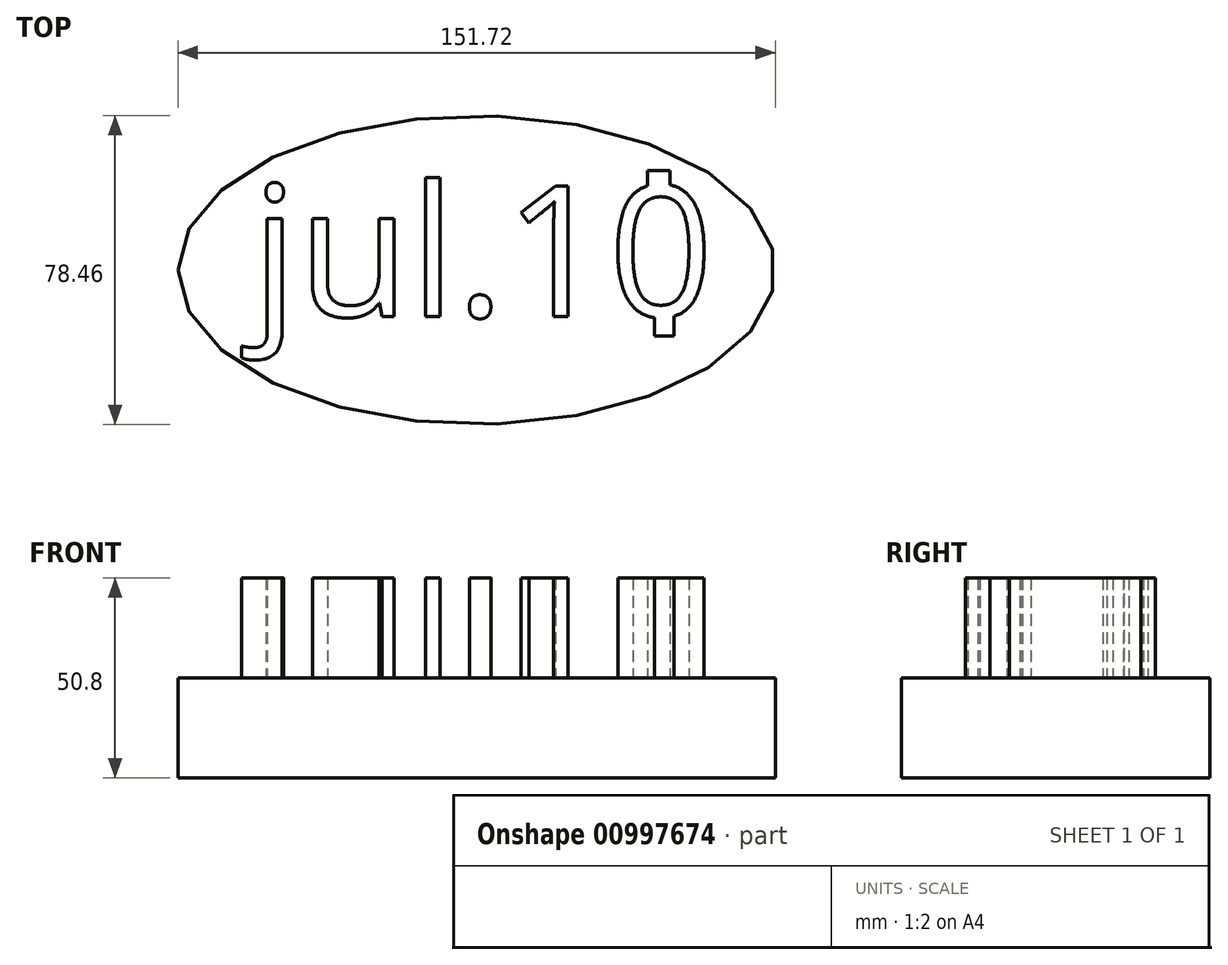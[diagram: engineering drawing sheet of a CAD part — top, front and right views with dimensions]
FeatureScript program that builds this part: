
annotation { "Feature Type Name" : "Feature", "Feature Type Description" : "" }
export const myFeature = defineFeature(function(context is Context, id is Id, definition is map)
    precondition{}
    {
        {
            var Q0;
            Q0=qCreatedBy(makeId("Top.planeOp"),FACE);
            var sketch = newSketch(context, id + "F0", { "sketchPlane" : qUnion([Q0])});
            skEllipse(sketch, "E0", {"center": v(0, 0) * mm, "majorRadius": 75.86 * mm, "minorRadius": 39.23 * mm, "majorAxis": v(-1, 0)});
            skSolve(sketch);
        }
        {
            var Q0;
            Q0 = qSketchRegion(id + "F0", true);
            extrude(context, id + "F1", {"entities" : qUnion([Q0]), "depth" : 25.4 * mm, "offsetDistance" : 25.4 * mm});
        }
        {
            var Q0;
            Q0=makeQuery(id+"F1.opExtrude","CAP_FACE",FACE,{"disambiguationData":[OSD([sQuery(id+"F0.wireOp",EDGE,"E0")])],"isStart":false});
            var sketch = newSketch(context, id + "F2", { "sketchPlane" : qUnion([Q0])});
            skText(sketch, "E1", { "text": "jul.10", "fontName": "OpenSans-Regular.ttf"});
            skLineSegment(sketch, "E2.bottom", {"start": v(43.33, 25.3) * mm, "end": v(49.1, 25.3) * mm});
            skLineSegment(sketch, "E2.top", {"start": v(43.33, 13.15) * mm, "end": v(49.1, 13.15) * mm});
            skLineSegment(sketch, "E2.left", {"start": v(43.33, 25.3) * mm, "end": v(43.33, 13.15) * mm});
            skLineSegment(sketch, "E2.right", {"start": v(49.1, 25.3) * mm, "end": v(49.1, 13.15) * mm});
            skLineSegment(sketch, "E3.bottom", {"start": v(45.11, -4.11) * mm, "end": v(50.15, -4.11) * mm});
            skLineSegment(sketch, "E3.top", {"start": v(45.11, -16.72) * mm, "end": v(50.15, -16.72) * mm});
            skLineSegment(sketch, "E3.left", {"start": v(45.11, -4.11) * mm, "end": v(45.11, -16.72) * mm});
            skLineSegment(sketch, "E3.right", {"start": v(50.15, -4.11) * mm, "end": v(50.15, -16.72) * mm});
            const initialGuessF2  = {"E1": [-0.0572, -0.01175, 1, 0, 0.03338]};
            skSetInitialGuess(sketch, initialGuessF2);
            skSolve(sketch);
        }
        {
            var Q0;
            Q0 = qSketchRegion(id + "F2", true);
            extrude(context, id + "F3", {"entities" : qUnion([Q0]), "operationType" : NewBodyOperationType.ADD, "depth" : 25.4 * mm, "offsetDistance" : 25.4 * mm});
        }
    });
